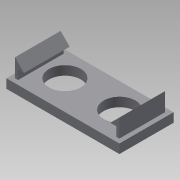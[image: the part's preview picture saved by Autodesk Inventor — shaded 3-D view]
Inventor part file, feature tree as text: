
AUTODESK INVENTOR PART (.ipt)
format: ipt  version: 2015 SP1 (Build 190203100, 203)  size: 146,944 bytes
history: native  units: mm
features: extrude x4, sketch x4, projected_geometry x2
ambient origin geometry x8: Origin, YZ Plane, XZ Plane, XY Plane, X Axis, Y Axis, Z Axis, Center Point
bodies: Solid1 (feature_tree)
feature tree (10):
  extrude  "Extrusion1"  Depth=3.0mm
  extrude  "Extrusion2"  Depth=32.35mm
  extrude  "Extrusion3"  Depth=15.0mm
  extrude  "Extrusion4"  Depth=3.0mm
  sketch  "Sketch1"  dims[d0=3.0mm d1=0.0mm d2=10.5mm]
  sketch  "Sketch2"  dims[d3=32.35mm d4=32.35mm]
  projected_geometry  "Projected Loop1"
  sketch  "Sketch3"  dims[d5=16.175mm d6=15.0mm]
  sketch  "Sketch4"  dims[d7=15.0mm d8=12.5mm d9=18.0mm d12=9.0mm d13=9.0mm d14=10.5mm d15=6.75mm d16=6.75mm d17=1.0mm d18=1.0mm d19=6.0mm d20=0.0mm d21=45.0deg d22=3.0mm d23=45.0deg d24=15.0mm d25=0.0mm d26=2.0mm d27=45.0deg d28=2.0mm d29=45.0deg d30=2.0mm d31=135.0deg d32=180.0deg d33=3.0mm d34=0.0mm d35=3.0mm]
  projected_geometry  "Projected Loop2"
